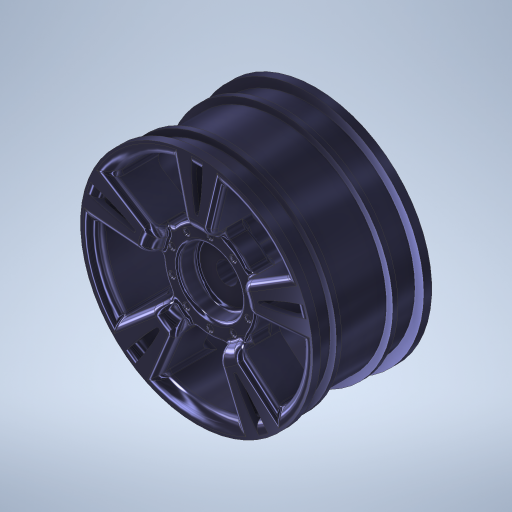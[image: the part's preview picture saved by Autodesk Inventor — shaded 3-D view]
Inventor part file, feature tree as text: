
AUTODESK INVENTOR PART (.ipt)
format: ipt  version: 2023.1 (Build 271208000, 208)  size: 2,130,432 bytes
history: native  units: in
note: dims shown in document units (in); Inventor stores cm internally (conversion verified against a paired STEP export)
features: fillet x14, sketch x14, projected_geometry x8, extrude x7, revolve x6, pattern_circular x3, other x3, plane x2, hole x1
ambient origin geometry x8: Origin, YZ Plane, XZ Plane, XY Plane, X Axis, Y Axis, Z Axis, Center Point
bodies: Solid1 (feature_tree)
feature tree (58):
  revolve  "Revolution1"  [1 undecoded]
  revolve  "Revolution2"  [1 undecoded]
  revolve  "Revolution3"  [1 undecoded]
  extrude  "Extrusion1"  Depth=0.275in
  extrude  "Extrusion2"  Depth=0.275in
  extrude  "Extrusion3"  TaperAngle=90.0deg  [1 undecoded]
  fillet  "Fillet1"  Radius=1.8in
  extrude  "Extrusion4"  Depth=0.66in
  fillet  "Fillet2"  Radius=0.465in
  pattern_circular  "Circular Pattern1"  [2 undecoded]
  revolve  "Revolution4"  [1 undecoded]
  revolve  "Revolution5"  [1 undecoded]
  fillet  "Fillet3"  Radius=1.9685in
  other  "Work Point1"
  plane  "Work Plane1"
  revolve  "Revolution6"  Angle=360.0deg
  fillet  "Fillet4"  Radius=0.05in
  fillet  "Fillet5"  [1 undecoded]
  fillet  "Fillet6"  Radius=0.5841in
  fillet  "Fillet7"  Radius=0.063in
  fillet  "Fillet8"  Radius=0.125in
  fillet  "Fillet9"  [1 undecoded]
  extrude  "Extrusion5"  Depth=0.032in
  fillet  "Fillet10"  Radius=0.154in
  extrude  "Extrusion6"  Depth=0.032in
  pattern_circular  "Circular Pattern2"  [2 undecoded]
  fillet  "Fillet11"  Radius=0.1407in
  hole  "Hole1"  [1 undecoded]
  plane  "Work Plane2"
  extrude  "Extrusion7"  TaperAngle=90.0deg  [1 undecoded]
  fillet  "Fillet12"  Radius=0.0625in
  pattern_circular  "Circular Pattern3"  [2 undecoded]
  fillet  "Fillet13"  Radius=0.032in
  fillet  "Fillet14"  Radius=0.032in
  sketch  "Sketch1"  dims[d0=2.045in d1=1.045in]
  sketch  "Sketch2"  dims[d2=90.0deg d3=0.07in]
  sketch  "Sketch3"  dims[d4=0.07in d5=1.885in]
  sketch  "Sketch4"  dims[d6=90.0deg d7=0.275in]
  sketch  "Sketch5"  dims[d8=0.045in d10=0.275in]
  sketch  "Sketch6"  dims[d11=2.0in d12=90.0deg d13=1.8in]
  projected_geometry  "Projected Loop1"
  sketch  "Sketch7"  dims[d14=0.465in d15=0.0in d16=0.66in d17=0.465in d18=0.0in]
  sketch  "Sketch8"  dims[d19=0.265in d20=0.0in]
  sketch  "Sketch9"  dims[d21=0.1in]
  other  "Work Point2"
  other  "Work Point3"
  sketch  "Sketch10"  dims[d22=0.1855in]
  sketch  "Sketch12"  dims[d23=0.1875in]
  sketch  "Sketch13"  dims[d24=0.3in]
  projected_geometry  "Projected Loop2"
  sketch  "Sketch14"  dims[d25=2.25in]
  sketch  "Sketch15"  dims[d26=0.5in d27=0.05in d28=0.36in d29=0.0in d30=0.0156in d31=1.9685in d32=360.0deg d34=0.05in d35=90.0deg d36=0.5841in d37=0.063in d38=0.125in d39=90.0deg d40=0.2in d45=0.154in d46=0.05in d47=0.265in d48=0.1407in d49=0.2in d50=90.0deg d51=0.0625in d52=0.0625in d53=0.032in d54=0.032in d55=0.032in d56=0.032in d59=0.475in d60=0.2in d61=0.0in d62=0.125in d63=0.1443in d67=0.05in d68=0.05in d69=0.5375in d70=1.0in d71=0.0in d72=1.9685in d73=360.0deg d75=0.032in d76=0.1875in d77=0.75in d78=0.375in d79=0.25in d80=0.5635in d81=1.0in d82=0.8108in d83=-0.015in d84=0.7in d85=0.05in d86=1.0in d87=0.1374in d88=0.005in d89=3.937in d90=360.0deg d92=0.032in d93=0.032in]
  projected_geometry  "Project Cut Edges1"
  projected_geometry  "Project Cut Edges2"
  projected_geometry  "Project Cut Edges3"
  projected_geometry  "Project Cut Edges4"
  projected_geometry  "Project Cut Edges5"
  projected_geometry  "Project Cut Edges6"
note: 16 required parameter values undecoded (feature->parameter linkage not recoverable at this tier; creation-order binding heuristic only, values carry confidence <= 0.55)